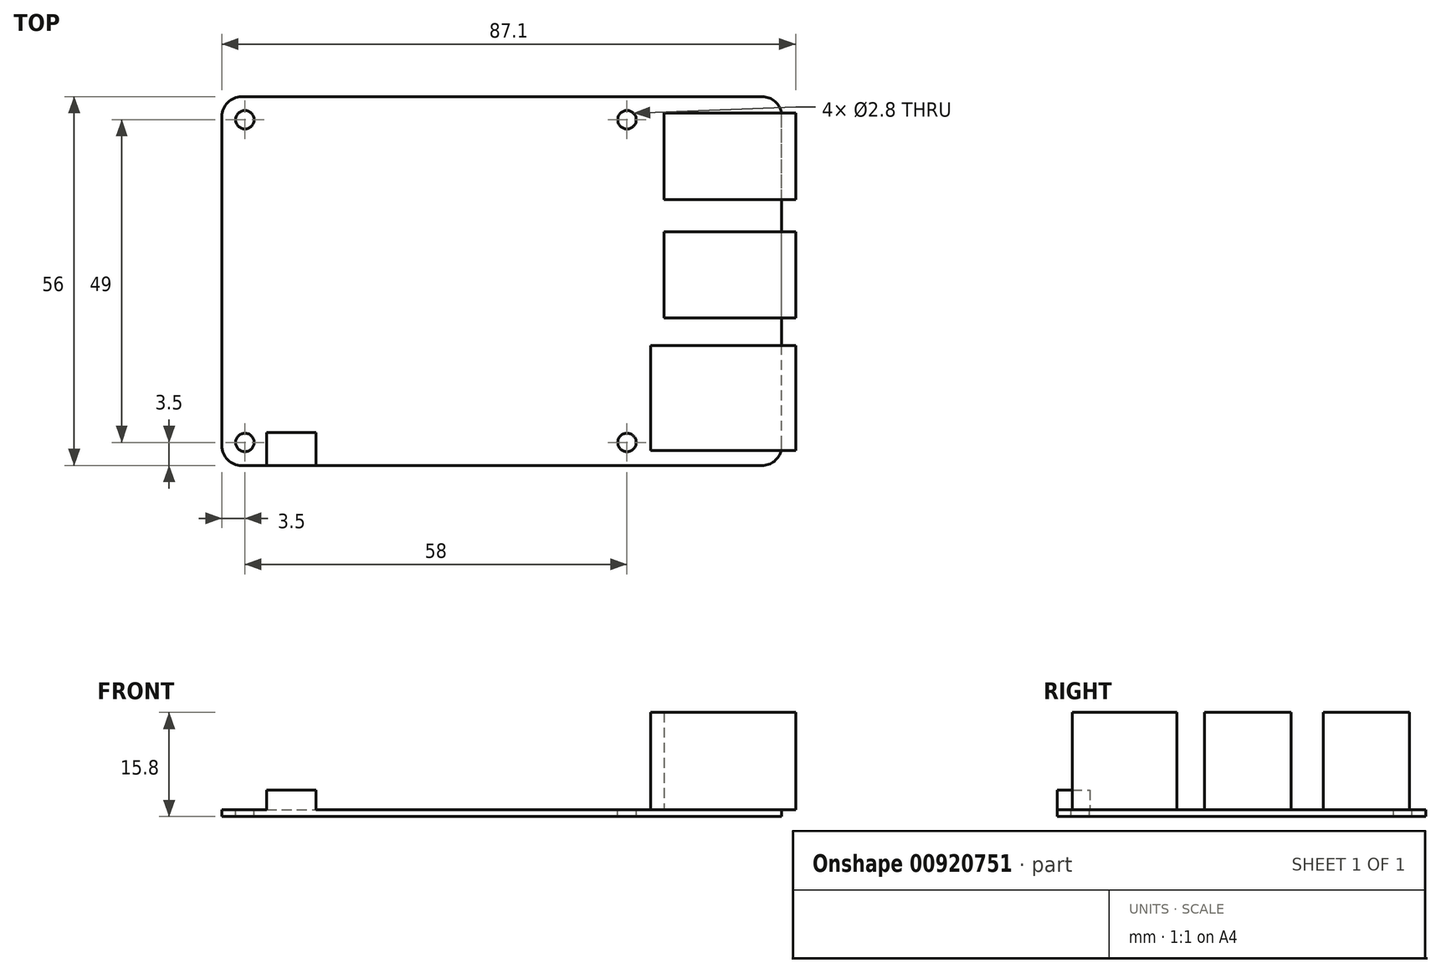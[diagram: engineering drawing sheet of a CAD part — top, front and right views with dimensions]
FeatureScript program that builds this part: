
annotation { "Feature Type Name" : "Feature", "Feature Type Description" : "" }
export const myFeature = defineFeature(function(context is Context, id is Id, definition is map)
    precondition{}
    {
        {
            var Q0;
            Q0=qCreatedBy(makeId("Top.planeOp"),FACE);
            var sketch = newSketch(context, id + "F0", { "sketchPlane" : qUnion([Q0])});
            skLineSegment(sketch, "E0.bottom", {"start": v(-42.5, -28) * mm, "end": v(42.5, -28) * mm});
            skLineSegment(sketch, "E0.top", {"start": v(-42.5, 28) * mm, "end": v(42.5, 28) * mm});
            skLineSegment(sketch, "E0.left", {"start": v(-42.5, -28) * mm, "end": v(-42.5, 28) * mm});
            skLineSegment(sketch, "E0.right", {"start": v(42.5, -28) * mm, "end": v(42.5, 28) * mm});
            skSolve(sketch);
        }
        {
            var Q0;
            Q0 = qSketchRegion(id + "F0", true);
            extrude(context, id + "F1", {"entities" : qUnion([Q0]), "depth" : 1 * mm, "offsetDistance" : 25 * mm});
        }
        {
            var Q0;
            Q0=makeQuery(id+"F1.opExtrude","SWEPT_EDGE",EDGE,{"disambiguationData":[OSD([sQuery(id+"F0.wireOp",EDGE,"E0.bottom"),sQuery(id+"F0.wireOp",EDGE,"E0.right")])]});
            var Q1;
            Q1=makeQuery(id+"F1.opExtrude","SWEPT_EDGE",EDGE,{"disambiguationData":[OSD([sQuery(id+"F0.wireOp",EDGE,"E0.top"),sQuery(id+"F0.wireOp",EDGE,"E0.right")])]});
            var Q2;
            Q2=makeQuery(id+"F1.opExtrude","SWEPT_EDGE",EDGE,{"disambiguationData":[OSD([sQuery(id+"F0.wireOp",EDGE,"E0.top"),sQuery(id+"F0.wireOp",EDGE,"E0.left")])]});
            var Q3;
            Q3=makeQuery(id+"F1.opExtrude","SWEPT_EDGE",EDGE,{"disambiguationData":[OSD([sQuery(id+"F0.wireOp",EDGE,"E0.bottom"),sQuery(id+"F0.wireOp",EDGE,"E0.left")])]});
            fillet(context, id + "F2", {"entities" : qUnion([Q0, Q1, Q2, Q3]), "radius" : 3 * mm, "tangentPropagation" : true, "allowEdgeOverflow" : false});
        }
        {
            var Q0;
            Q0=makeQuery(id+"F1.opExtrude","CAP_FACE",FACE,{"disambiguationData":[OSD([sQuery(id+"F0.wireOp",EDGE,"E0.bottom"),sQuery(id+"F0.wireOp",EDGE,"E0.top"),sQuery(id+"F0.wireOp",EDGE,"E0.left"),sQuery(id+"F0.wireOp",EDGE,"E0.right")])],"isStart":false});
            var sketch = newSketch(context, id + "F3", { "sketchPlane" : qUnion([Q0])});
            skLineSegment(sketch, "E1.bottom", {"start": v(44.6, -25.7) * mm, "end": v(22.6, -25.7) * mm});
            skLineSegment(sketch, "E1.top", {"start": v(44.6, -9.8) * mm, "end": v(22.6, -9.8) * mm});
            skLineSegment(sketch, "E1.left", {"start": v(44.6, -25.7) * mm, "end": v(44.6, -9.8) * mm});
            skLineSegment(sketch, "E1.right", {"start": v(22.6, -25.7) * mm, "end": v(22.6, -9.8) * mm});
            skLineSegment(sketch, "E2.bottom", {"start": v(24.6, 7.5) * mm, "end": v(44.6, 7.5) * mm});
            skLineSegment(sketch, "E2.top", {"start": v(24.6, -5.6) * mm, "end": v(44.6, -5.6) * mm});
            skLineSegment(sketch, "E2.left", {"start": v(24.6, 7.5) * mm, "end": v(24.6, -5.6) * mm});
            skLineSegment(sketch, "E2.right", {"start": v(44.6, 7.5) * mm, "end": v(44.6, -5.6) * mm});
            skLineSegment(sketch, "E3.bottom", {"start": v(24.6, 25.5) * mm, "end": v(44.6, 25.5) * mm});
            skLineSegment(sketch, "E3.top", {"start": v(24.6, 12.4) * mm, "end": v(44.6, 12.4) * mm});
            skLineSegment(sketch, "E3.left", {"start": v(24.6, 25.5) * mm, "end": v(24.6, 12.4) * mm});
            skLineSegment(sketch, "E3.right", {"start": v(44.6, 25.5) * mm, "end": v(44.6, 12.4) * mm});
            skSolve(sketch);
        }
        {
            var Q0;
            Q0 = qSketchRegion(id + "F3", true);
            extrude(context, id + "F4", {"entities" : qUnion([Q0]), "operationType" : NewBodyOperationType.ADD, "depth" : 14.8 * mm, "offsetDistance" : 25 * mm});
        }
        {
            var Q0;
            Q0=makeQuery(id+"F1.opExtrude","CAP_FACE",FACE,{"disambiguationData":[OSD([sQuery(id+"F0.wireOp",EDGE,"E0.bottom"),sQuery(id+"F0.wireOp",EDGE,"E0.top"),sQuery(id+"F0.wireOp",EDGE,"E0.left"),sQuery(id+"F0.wireOp",EDGE,"E0.right")])],"isStart":false});
            var sketch = newSketch(context, id + "F5", { "sketchPlane" : qUnion([Q0])});
            skPoint(sketch, "E4", {"position": v(-39, 24.5) * mm});
            skPoint(sketch, "E5", {"position": v(-39, -24.5) * mm});
            skPoint(sketch, "E6", {"position": v(19, -24.5) * mm});
            skPoint(sketch, "E7", {"position": v(19, 24.5) * mm});
            skSolve(sketch);
        }
        {
            var Q0;
            Q0=sQuery(id+"F5.wireOp",VERTEX,"E4");
            var Q1;
            Q1=sQuery(id+"F5.wireOp",VERTEX,"E7");
            var Q2;
            Q2=sQuery(id+"F5.wireOp",VERTEX,"E6");
            var Q3;
            Q3=sQuery(id+"F5.wireOp",VERTEX,"E5");
            var Q4;
            Q4=makeQuery(id+"F1.opExtrude","SWEPT_BODY",BODY,{"disambiguationData":[OSD([sQuery(id+"F0.wireOp",EDGE,"E0.bottom"),sQuery(id+"F0.wireOp",EDGE,"E0.top"),sQuery(id+"F0.wireOp",EDGE,"E0.left"),sQuery(id+"F0.wireOp",EDGE,"E0.right")])]});
            hole(context, id + "F6", {"style" : HoleStyle.SIMPLE, "endStyle" : HoleEndStyle.BLIND, "holeDiameter" : 2.8 * mm, "majorDiameter" : 5 * mm, "holeDepth" : 5 * mm, "isTappedThrough" : true, "tappedDepth" : 12 * mm, "tapClearance" : 3, "locations" : qUnion([Q0, Q1, Q2, Q3]), "scope" : qUnion([Q4])});
        }
        {
            var Q0;
            Q0=makeQuery(id+"F1.opExtrude","CAP_FACE",FACE,{"disambiguationData":[OSD([sQuery(id+"F0.wireOp",EDGE,"E0.bottom"),sQuery(id+"F0.wireOp",EDGE,"E0.top"),sQuery(id+"F0.wireOp",EDGE,"E0.left"),sQuery(id+"F0.wireOp",EDGE,"E0.right")])],"isStart":false});
            var sketch = newSketch(context, id + "F7", { "sketchPlane" : qUnion([Q0])});
            skLineSegment(sketch, "E8.bottom", {"start": v(-35.7, -28) * mm, "end": v(-28.2, -28) * mm});
            skLineSegment(sketch, "E8.top", {"start": v(-35.7, -23) * mm, "end": v(-28.2, -23) * mm});
            skLineSegment(sketch, "E8.left", {"start": v(-35.7, -28) * mm, "end": v(-35.7, -23) * mm});
            skLineSegment(sketch, "E8.right", {"start": v(-28.2, -28) * mm, "end": v(-28.2, -23) * mm});
            skSolve(sketch);
        }
        {
            var Q0;
            Q0 = qSketchRegion(id + "F7", true);
            extrude(context, id + "F8", {"entities" : qUnion([Q0]), "operationType" : NewBodyOperationType.ADD, "depth" : 3 * mm, "offsetDistance" : 25 * mm});
        }
    });
